# Revit family: Polar_Double_Undermount
name_source: partatom
category: Plumbing Fixtures
revit_build: Autodesk Revit 2016 (Build: 20161004_0715(x64)
units: mm (PartAtom-declared; Revit-internal decimal feet)

## family parameters
Cut with Voids When Loaded = No
Host = Face
OmniClass Number = 23.45.05.14.14
OmniClass Title = Sinks/Lavatories
Part Type = Normal
Room Calculation Point = No
Round Connector Dimension = Use Diameter
Shared = No

## types (1)
- POLAR DOUBLE BOWL UNDERMOUNT
    Assembly Code = D2010410
    Benchtop Depth = 20 mm
    CW Connection = No
    Default Elevation = 0 mm  [stored 0 ft]
    Description = Polar Double Bowl Undermount
    HW Connection = No
    Manufacturer = GWA Bathrooms & Kitchens
    Model = PPL20BU
    Sink = GWA_Metal-Stainless
    URL = https://www.clark.com.au
    Vent Connection = No

note: [stored X ft] marks values corroborated as IEEE doubles in the binary element streams (Revit-internal decimal feet)

## geometry (parser evidence)
native form markers: Sweep x3
no freeform markers — native parametric forms only
